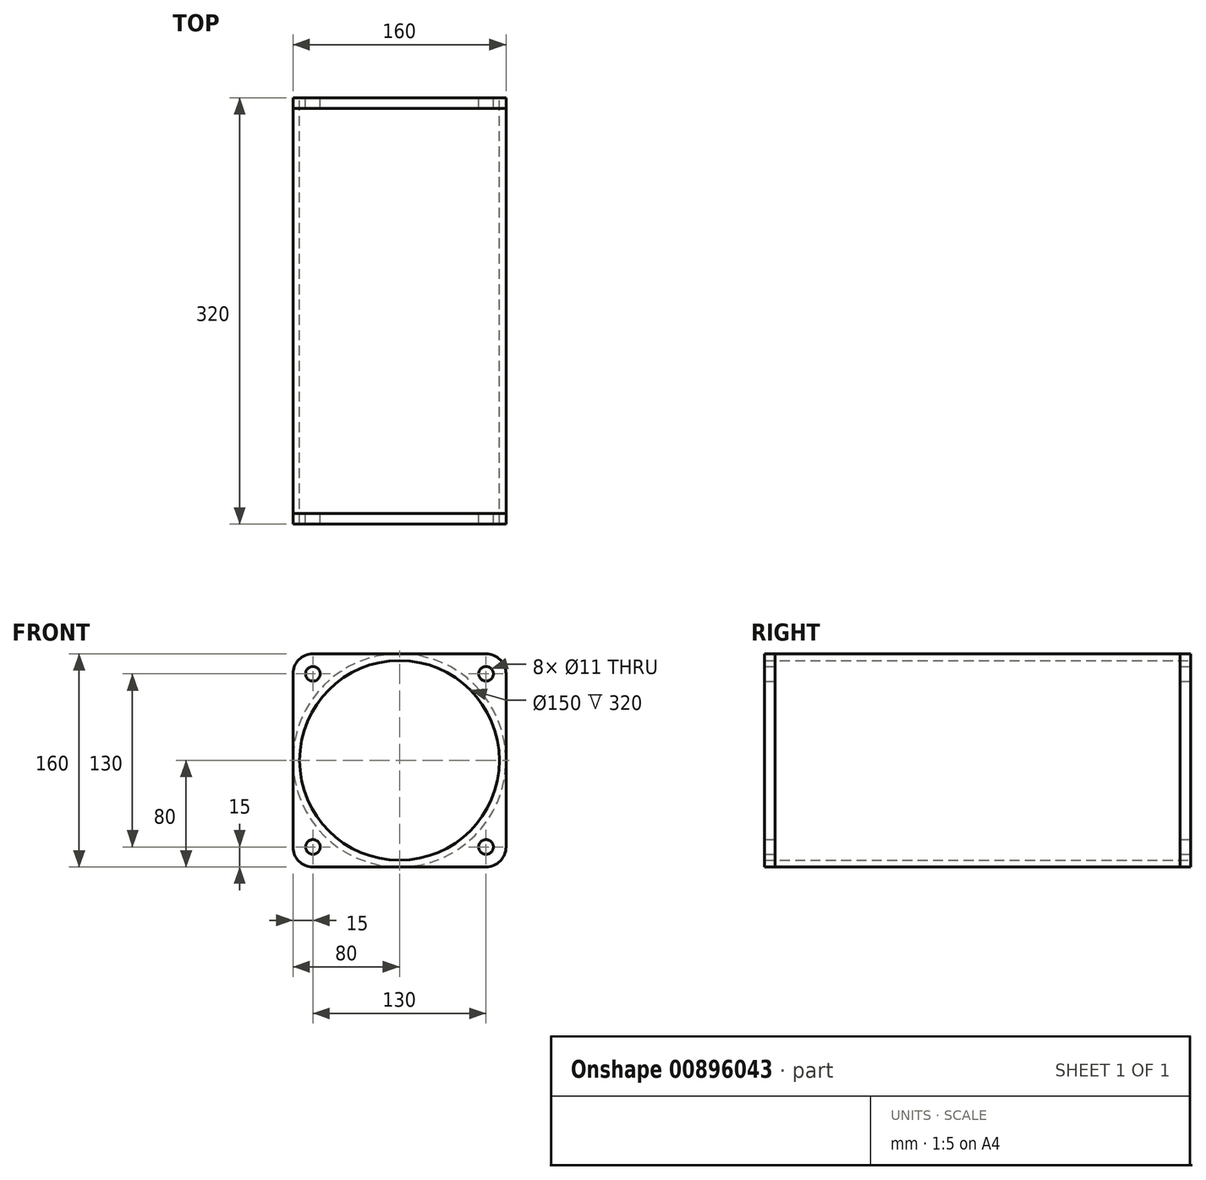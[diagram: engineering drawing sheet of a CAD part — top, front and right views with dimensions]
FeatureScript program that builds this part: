
annotation { "Feature Type Name" : "Feature", "Feature Type Description" : "" }
export const myFeature = defineFeature(function(context is Context, id is Id, definition is map)
    precondition{}
    {
        {
            var Q0;
            Q0=qCreatedBy(makeId("Front.planeOp"),FACE);
            cPlane(context, id + "F0", {"entities" : qUnion([Q0]), "cplaneType" : CPlaneType.OFFSET, "offset" : 320 * mm, "width" : 150 * mm, "height" : 150 * mm});
        }
        {
            var Q0;
            Q0=qCreatedBy(makeId("Front.planeOp"),FACE);
            var sketch = newSketch(context, id + "F1", { "sketchPlane" : qUnion([Q0])});
            skLineSegment(sketch, "E0.bottom", {"start": v(65, -80) * mm, "end": v(-65, -80) * mm});
            skLineSegment(sketch, "E0.top", {"start": v(65, 80) * mm, "end": v(-65, 80) * mm});
            skLineSegment(sketch, "E0.left", {"start": v(80, -65) * mm, "end": v(80, 65) * mm});
            skLineSegment(sketch, "E0.right", {"start": v(-80, -65) * mm, "end": v(-80, 65) * mm});
            skPoint(sketch, "E0.middle", {"position": v(0, 0) * mm});
            skPoint(sketch, "E1.visualSharp", {"position": v(-80, 80) * mm});
            skArc(sketch, "E1.filletArc", {"start": v(-65, 80) * mm, "mid": v(-75.6, 75.6) * mm, "end": v(-80, 65) * mm});
            skPoint(sketch, "E2.visualSharp", {"position": v(80, 80) * mm});
            skArc(sketch, "E2.filletArc", {"start": v(80, 65) * mm, "mid": v(75.6, 75.6) * mm, "end": v(65, 80) * mm});
            skPoint(sketch, "E3.visualSharp", {"position": v(80, -80) * mm});
            skArc(sketch, "E3.filletArc", {"start": v(65, -80) * mm, "mid": v(75.6, -75.6) * mm, "end": v(80, -65) * mm});
            skPoint(sketch, "E4.visualSharp", {"position": v(-80, -80) * mm});
            skArc(sketch, "E4.filletArc", {"start": v(-80, -65) * mm, "mid": v(-75.6, -75.6) * mm, "end": v(-65, -80) * mm});
            skCircle(sketch, "E5", {"center": v(0, 0) * mm, "radius": 80 * mm});
            skCircle(sketch, "E6", {"center": v(0, 0) * mm, "radius": 75 * mm});
            skCircle(sketch, "E7", {"center": v(65, 65) * mm, "radius": 5.5 * mm});
            skCircle(sketch, "E8", {"center": v(-65, 65) * mm, "radius": 5.5 * mm});
            skCircle(sketch, "E9", {"center": v(65, -65) * mm, "radius": 5.5 * mm});
            skCircle(sketch, "E10", {"center": v(-65, -65) * mm, "radius": 5.5 * mm});
            skSolve(sketch);
        }
        {
            var Q0;
            Q0 = qSketchRegion(id + "F1", true);
            extrude(context, id + "F2", {"entities" : qUnion([Q0]), "depth" : 8 * mm, "offsetDistance" : 25 * mm});
        }
        {
            var Q0;
            Q0=makeQuery(id+"F1.imprint","IMPRINT",FACE,{"disambiguationData":[TD([[makeQuery(id+"F1.imprint","IMPRINT",EDGE,{"derivedFrom":sQuery(id+"F1.wireOp",EDGE,"E6")}),-1.0]])]});
            var Q1;
            Q1=qCreatedBy(id+"F0.planeOp",FACE);
            extrude(context, id + "F3", {"entities" : qUnion([Q0]), "operationType" : NewBodyOperationType.ADD, "endBound" : BoundingType.UP_TO_SURFACE, "depth" : 25 * mm, "endBoundEntityFace" : qUnion([Q1]), "offsetDistance" : 25 * mm});
        }
        {
            var Q0;
            {var subQ0=sQuery(id+"F1.wireOp",EDGE,"E3.filletArc");Q0=makeQuery(id+"F1.imprint","IMPRINT",FACE,{"disambiguationData":[TD([[makeQuery(id+"F1.imprint","IMPRINT",EDGE,{"derivedFrom":subQ0}),1.0]])]});}
            var Q1;
            {var subQ0=sQuery(id+"F1.wireOp",EDGE,"E4.filletArc");Q1=makeQuery(id+"F1.imprint","IMPRINT",FACE,{"disambiguationData":[TD([[makeQuery(id+"F1.imprint","IMPRINT",EDGE,{"derivedFrom":subQ0}),1.0]])]});}
            var Q2;
            {var subQ0=sQuery(id+"F1.wireOp",EDGE,"E2.filletArc");Q2=makeQuery(id+"F1.imprint","IMPRINT",FACE,{"disambiguationData":[TD([[makeQuery(id+"F1.imprint","IMPRINT",EDGE,{"derivedFrom":subQ0}),1.0]])]});}
            var Q3;
            {var subQ0=sQuery(id+"F1.wireOp",EDGE,"E1.filletArc");Q3=makeQuery(id+"F1.imprint","IMPRINT",FACE,{"disambiguationData":[TD([[makeQuery(id+"F1.imprint","IMPRINT",EDGE,{"derivedFrom":subQ0}),1.0]])]});}
            var Q4;
            Q4=qCreatedBy(id+"F0.planeOp",FACE);
            var Q5;
            Q5=qCreatedBy(id+"F0.planeOp",FACE);
            extrude(context, id + "F4", {"entities" : qUnion([Q0, Q1, Q2, Q3]), "operationType" : NewBodyOperationType.ADD, "endBound" : BoundingType.UP_TO_SURFACE, "depth" : 25 * mm, "endBoundEntityFace" : qUnion([Q4]), "offsetDistance" : 25 * mm, "hasSecondDirection" : true, "secondDirectionBound" : SecondDirectionBoundingType.UP_TO_SURFACE, "secondDirectionOppositeDirection" : false, "secondDirectionDepth" : 25 * mm, "secondDirectionBoundEntityFace" : qUnion([Q5]), "hasSecondDirectionOffset" : true, "secondDirectionOffsetDistance" : 8 * mm});
        }
    });
